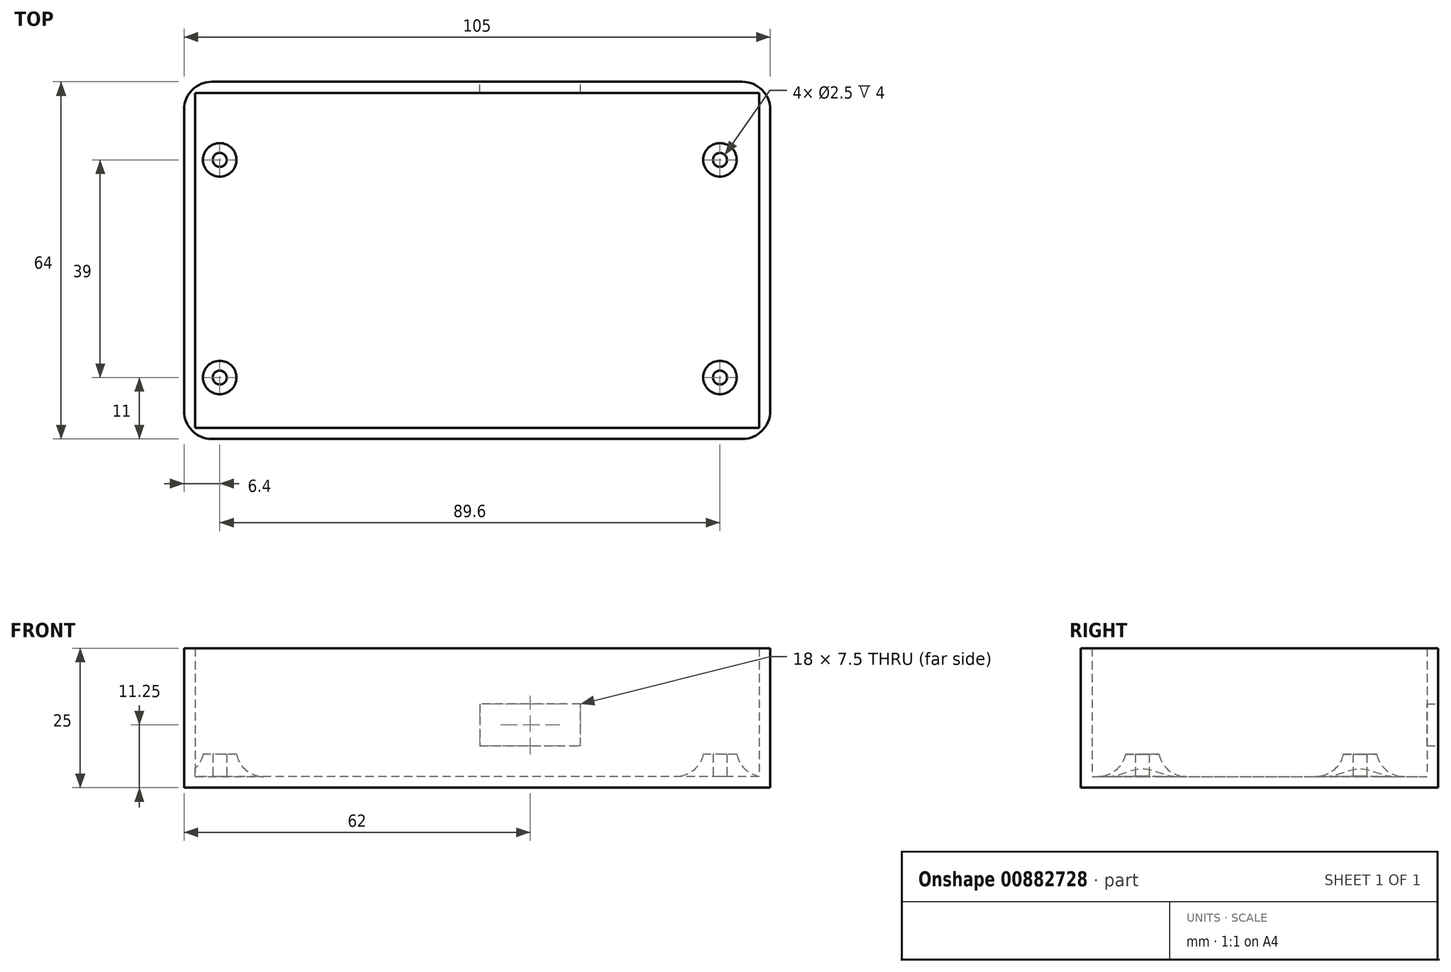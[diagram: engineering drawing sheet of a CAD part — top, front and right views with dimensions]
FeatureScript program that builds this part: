
annotation { "Feature Type Name" : "Feature", "Feature Type Description" : "" }
export const myFeature = defineFeature(function(context is Context, id is Id, definition is map)
    precondition{}
    {
        {
            var Q0;
            Q0=qCreatedBy(makeId("Top.planeOp"),FACE);
            var sketch = newSketch(context, id + "F0", { "sketchPlane" : qUnion([Q0])});
            skPoint(sketch, "E0.middle", {"position": v(0, 0) * mm});
            skLineSegment(sketch, "E1.bottom", {"start": v(50.5, -30) * mm, "end": v(-50.5, -30) * mm});
            skLineSegment(sketch, "E1.top", {"start": v(50.5, 30) * mm, "end": v(-50.5, 30) * mm});
            skLineSegment(sketch, "E1.left", {"start": v(50.5, -30) * mm, "end": v(50.5, 30) * mm});
            skLineSegment(sketch, "E1.right", {"start": v(-50.5, -30) * mm, "end": v(-50.5, 30) * mm});
            skSolve(sketch);
        }
        {
            var Q0;
            Q0=makeQuery(id+"F0.imprint","IMPRINT",FACE,{"disambiguationData":[TD([[makeQuery(id+"F0.imprint","IMPRINT",EDGE,{"derivedFrom":sQuery(id+"F0.wireOp",EDGE,"E1.bottom")}),-1.0]])]});
            extrude(context, id + "F1", {"entities" : qUnion([Q0]), "depth" : 2 * mm, "offsetDistance" : 25 * mm});
        }
        {
            var Q0;
            Q0=qCreatedBy(makeId("Top.planeOp"),FACE);
            var sketch = newSketch(context, id + "F2", { "sketchPlane" : qUnion([Q0])});
            skLineSegment(sketch, "E2.bottom", {"start": v(52.5, -32) * mm, "end": v(-52.5, -32) * mm});
            skLineSegment(sketch, "E2.top", {"start": v(52.5, 32) * mm, "end": v(-52.5, 32) * mm});
            skLineSegment(sketch, "E2.left", {"start": v(52.5, -32) * mm, "end": v(52.5, 32) * mm});
            skLineSegment(sketch, "E2.right", {"start": v(-52.5, -32) * mm, "end": v(-52.5, 32) * mm});
            skPoint(sketch, "E2.middle", {"position": v(0, 0) * mm});
            skLineSegment(sketch, "E3.bottom", {"start": v(50.5, -30) * mm, "end": v(-50.5, -30) * mm});
            skLineSegment(sketch, "E3.top", {"start": v(50.5, 30) * mm, "end": v(-50.5, 30) * mm});
            skLineSegment(sketch, "E3.left", {"start": v(50.5, -30) * mm, "end": v(50.5, 30) * mm});
            skLineSegment(sketch, "E3.right", {"start": v(-50.5, -30) * mm, "end": v(-50.5, 30) * mm});
            skSolve(sketch);
        }
        {
            var Q0;
            Q0=makeQuery(id+"F2.imprint","IMPRINT",FACE,{"disambiguationData":[TD([[makeQuery(id+"F2.imprint","IMPRINT",EDGE,{"derivedFrom":sQuery(id+"F2.wireOp",EDGE,"E2.bottom")}),-1.0]])]});
            extrude(context, id + "F3", {"entities" : qUnion([Q0]), "operationType" : NewBodyOperationType.ADD, "depth" : 25 * mm, "offsetDistance" : 25 * mm});
        }
        {
            var Q0;
            Q0=qCreatedBy(makeId("Top.planeOp"),FACE);
            var sketch = newSketch(context, id + "F4", { "sketchPlane" : qUnion([Q0])});
            skLineSegment(sketch, "E4", {"start": v(-58.38, -21) * mm, "end": v(57.85, -21) * mm, "construction": true});
            skLineSegment(sketch, "E5", {"start": v(-46.1, -43.8) * mm, "end": v(-46.1, 70.48) * mm, "construction": true});
            skLineSegment(sketch, "E6", {"start": v(-58.91, 18) * mm, "end": v(61.07, 18) * mm, "construction": true});
            skLineSegment(sketch, "E7", {"start": v(43.5, -45.6) * mm, "end": v(43.5, 43.42) * mm, "construction": true});
            skCircle(sketch, "E8", {"center": v(-46.1, 18) * mm, "radius": 1.25 * mm});
            skPoint(sketch, "E8.centerSnap0", {"position": v(-46.1, 13.34) * mm});
            skCircle(sketch, "E9", {"center": v(43.5, 18) * mm, "radius": 1.25 * mm});
            skCircle(sketch, "E10", {"center": v(43.5, -21) * mm, "radius": 1.25 * mm});
            skCircle(sketch, "E11", {"center": v(-46.1, -21) * mm, "radius": 1.25 * mm});
            skCircle(sketch, "E12", {"center": v(-46.1, 18) * mm, "radius": 3 * mm});
            skCircle(sketch, "E13", {"center": v(43.5, 18) * mm, "radius": 3 * mm});
            skCircle(sketch, "E14", {"center": v(43.5, -21) * mm, "radius": 3 * mm});
            skCircle(sketch, "E15", {"center": v(-46.1, -21) * mm, "radius": 3 * mm});
            skSolve(sketch);
        }
        {
            var Q0;
            Q0=makeQuery(id+"F4.imprint","IMPRINT",FACE,{"disambiguationData":[TD([[makeQuery(id+"F4.imprint","IMPRINT",EDGE,{"derivedFrom":sQuery(id+"F4.wireOp",EDGE,"E8")}),-1.0]])]});
            var Q1;
            Q1=makeQuery(id+"F4.imprint","IMPRINT",FACE,{"disambiguationData":[TD([[makeQuery(id+"F4.imprint","IMPRINT",EDGE,{"derivedFrom":sQuery(id+"F4.wireOp",EDGE,"E11")}),-1.0]])]});
            var Q2;
            Q2=makeQuery(id+"F4.imprint","IMPRINT",FACE,{"disambiguationData":[TD([[makeQuery(id+"F4.imprint","IMPRINT",EDGE,{"derivedFrom":sQuery(id+"F4.wireOp",EDGE,"E10")}),-1.0]])]});
            var Q3;
            Q3=makeQuery(id+"F4.imprint","IMPRINT",FACE,{"disambiguationData":[TD([[makeQuery(id+"F4.imprint","IMPRINT",EDGE,{"derivedFrom":sQuery(id+"F4.wireOp",EDGE,"E9")}),-1.0]])]});
            extrude(context, id + "F5", {"entities" : qUnion([Q0, Q1, Q2, Q3]), "operationType" : NewBodyOperationType.ADD, "depth" : 6 * mm, "offsetDistance" : 25 * mm});
        }
        {
            var Q0;
            Q0=makeQuery(id+"F3.opExtrude","SWEPT_FACE",FACE,{"disambiguationData":[OSD([sQuery(id+"F2.wireOp",EDGE,"E2.top")])]});
            var sketch = newSketch(context, id + "F6", { "sketchPlane" : qUnion([Q0])});
            skLineSegment(sketch, "E16", {"start": v(-0.5, 36.7) * mm, "end": v(-0.5, -12.46) * mm, "construction": true});
            skLineSegment(sketch, "E17", {"start": v(-18.5, 36.7) * mm, "end": v(-18.5, -12.46) * mm, "construction": true});
            skLineSegment(sketch, "E18", {"start": v(-73.7, 15) * mm, "end": v(72.67, 15) * mm, "construction": true});
            skLineSegment(sketch, "E19", {"start": v(-75.3, 7.5) * mm, "end": v(72.67, 7.5) * mm, "construction": true});
            skLineSegment(sketch, "E20", {"start": v(-18.5, 15) * mm, "end": v(-18.5, 7.5) * mm});
            skLineSegment(sketch, "E21", {"start": v(-18.5, 7.5) * mm, "end": v(-0.5, 7.5) * mm});
            skLineSegment(sketch, "E22", {"start": v(-0.5, 7.5) * mm, "end": v(-0.5, 15) * mm});
            skLineSegment(sketch, "E23", {"start": v(-0.5, 15) * mm, "end": v(-18.5, 15) * mm});
            skSolve(sketch);
        }
        {
            var Q0;
            Q0=makeQuery(id+"F6.imprint","IMPRINT",FACE,{"disambiguationData":[TD([[makeQuery(id+"F6.imprint","IMPRINT",EDGE,{"derivedFrom":sQuery(id+"F6.wireOp",EDGE,"E20")}),1.0]])]});
            extrude(context, id + "F7", {"entities" : qUnion([Q0]), "operationType" : NewBodyOperationType.REMOVE, "oppositeDirection" : true, "depth" : 5 * mm, "offsetDistance" : 25 * mm});
        }
        {
            var Q0;
            Q0=makeQuery(id+"F3.opExtrude","SWEPT_EDGE",EDGE,{"disambiguationData":[OSD([sQuery(id+"F2.wireOp",EDGE,"E2.top"),sQuery(id+"F2.wireOp",EDGE,"E2.right")])]});
            var Q1;
            Q1=makeQuery(id+"F3.opExtrude","SWEPT_EDGE",EDGE,{"disambiguationData":[OSD([sQuery(id+"F2.wireOp",EDGE,"E2.bottom"),sQuery(id+"F2.wireOp",EDGE,"E2.right")])]});
            var Q2;
            Q2=makeQuery(id+"F3.opExtrude","SWEPT_EDGE",EDGE,{"disambiguationData":[OSD([sQuery(id+"F2.wireOp",EDGE,"E2.bottom"),sQuery(id+"F2.wireOp",EDGE,"E2.left")])]});
            var Q3;
            Q3=makeQuery(id+"F3.opExtrude","SWEPT_EDGE",EDGE,{"disambiguationData":[OSD([sQuery(id+"F2.wireOp",EDGE,"E2.top"),sQuery(id+"F2.wireOp",EDGE,"E2.left")])]});
            var Q4;
            Q4=makeQuery(id+"F5.boolean.opBoolean","INTERSECT",EDGE,{"derivedFrom":[makeQuery(id+"F1.opExtrude","CAP_FACE",FACE,{"disambiguationData":[OSD([sQuery(id+"F0.wireOp",EDGE,"E1.bottom"),sQuery(id+"F0.wireOp",EDGE,"E1.top"),sQuery(id+"F0.wireOp",EDGE,"E1.left"),sQuery(id+"F0.wireOp",EDGE,"E1.right")])],"isStart":false}),makeQuery(id+"F5.opExtrude","SWEPT_FACE",FACE,{"disambiguationData":[OSD([sQuery(id+"F4.wireOp",EDGE,"E14")])]})]});
            var Q5;
            Q5=makeQuery(id+"F5.boolean.opBoolean","INTERSECT",EDGE,{"derivedFrom":[makeQuery(id+"F1.opExtrude","CAP_FACE",FACE,{"disambiguationData":[OSD([sQuery(id+"F0.wireOp",EDGE,"E1.bottom"),sQuery(id+"F0.wireOp",EDGE,"E1.top"),sQuery(id+"F0.wireOp",EDGE,"E1.left"),sQuery(id+"F0.wireOp",EDGE,"E1.right")])],"isStart":false}),makeQuery(id+"F5.opExtrude","SWEPT_FACE",FACE,{"disambiguationData":[OSD([sQuery(id+"F4.wireOp",EDGE,"E13")])]})]});
            var Q6;
            Q6=makeQuery(id+"F5.boolean.opBoolean","INTERSECT",EDGE,{"derivedFrom":[makeQuery(id+"F1.opExtrude","CAP_FACE",FACE,{"disambiguationData":[OSD([sQuery(id+"F0.wireOp",EDGE,"E1.bottom"),sQuery(id+"F0.wireOp",EDGE,"E1.top"),sQuery(id+"F0.wireOp",EDGE,"E1.left"),sQuery(id+"F0.wireOp",EDGE,"E1.right")])],"isStart":false}),makeQuery(id+"F5.opExtrude","SWEPT_FACE",FACE,{"disambiguationData":[OSD([sQuery(id+"F4.wireOp",EDGE,"E15")])]})]});
            var Q7;
            Q7=makeQuery(id+"F5.boolean.opBoolean","INTERSECT",EDGE,{"derivedFrom":[makeQuery(id+"F1.opExtrude","CAP_FACE",FACE,{"disambiguationData":[OSD([sQuery(id+"F0.wireOp",EDGE,"E1.bottom"),sQuery(id+"F0.wireOp",EDGE,"E1.top"),sQuery(id+"F0.wireOp",EDGE,"E1.left"),sQuery(id+"F0.wireOp",EDGE,"E1.right")])],"isStart":false}),makeQuery(id+"F5.opExtrude","SWEPT_FACE",FACE,{"disambiguationData":[OSD([sQuery(id+"F4.wireOp",EDGE,"E12")])]})]});
            fillet(context, id + "F8", {"entities" : qUnion([Q0, Q1, Q2, Q3, Q4, Q5, Q6, Q7]), "radius" : 5 * mm, "tangentPropagation" : true, "allowEdgeOverflow" : false});
        }
    });
